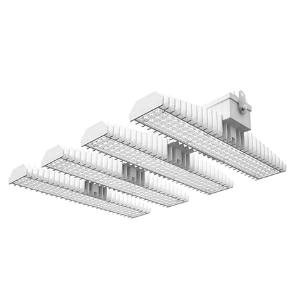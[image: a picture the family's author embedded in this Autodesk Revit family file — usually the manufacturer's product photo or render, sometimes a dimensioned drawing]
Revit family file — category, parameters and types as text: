
# Revit family: 3f_filippi_-_3f_lem_concentrato_3f_filippi_-_58890_a0811_-_3f_lem_4_led_200_cr_conc___vt_7c4e
name_source: partatom
category: Lighting Fixtures
units: mm (PartAtom-declared; Revit-internal decimal feet)

## family parameters
Cut with Voids When Loaded = No
Host = Face
Light Source = No
Part Type = Normal
Room Calculation Point = No
Round Connector Dimension = Use Diameter
Shared = No

## types (1)
- 3F Filippi - 3F LEM Concentrato (1 x LED, 30311 lm, 218 W, 4000 K)
    Apparent Load = 218 VA
    Approval mark = CE
    CIE Flux Codes = 83 96 99 100 100
    Color Rendering = 80
    Color Temperature = 4000 K
    Control Gear = Electronic ballast
    Default Elevation = 1800 mm
    Description = Industrial luminaire with high light output and high luminous efficiency designed with the most innovative technologies for environments with temperature up to 55°C.

ILLUMINOTECHNICAL
Luminous efficiency 100% (DLOR 99%, ULOR 1%).
Initial luminous flux of the luminaire 30311 lm.
Direct symmetric narrow distribution: the illuminated area has a elliptical shape.
Installation Interdistance Transv.D = 0.52 x hu - Long.D = 1.16 x hu.
Tabular UGR (CIE 117 - 4H-8H; S=0.25H; 70/50/20): RUG 17.2 - 21.
Beam angle: 31° - 73°.
Luminous efficacy 139 lm/W.
Lifetime (L93/B10): 30000 h. (tq+25°C)
Lifetime (L90/B10): 50000 h. (tq+25°C)
Lifetime (L85/B10): 80000 h. (tq+25°C)
Lifetime (L80/B10): 100000 h. (tq+25°C)
Lifetime (L85/B10): 50000 h. (tq+55°C)
Sudden decreased luminous flux after 50000 hours: 0% (C0).
Photobiological safety in compliance with IEC/TR 62778: RG0 risk exempt, (IEC 62471).
In compliance with IEC/EN 62722-2-1 - IEC/EN 62717 standards.

SOURCE
4 Mid-Power linear LED modules 50W/840.
Energy efficiency class (UE 2019/2020 - UE 2019/2015): C.
CIE 13.3 Colour rendering index: CRI >80 (R9 <50%).
IES TM-30 Fidelity Index: Rf = 84 Rg = 95.
CCT nominal colour temperature 4000 K.
Colour initial tolerance (MacAdam): SDCM 3.

MECHANICAL
Passive modular heatsinks in die-casted aluminium, painted in white colour.
To optimize the thermal management of the LED module, the heatsinks are oversized and provided with self-cleaning of cooling fins.
Wiring body in aluminium and galvanised steel anchored solidly to the sinks and thermally separated.
3F Lens lenses with high luminous efficiency, transparent methacrylate (PMMA), fixed to the LED modules.
Fixing brackets in stainless steel.
Luminaire with limited surface temperature. - D - (EN 60598-2-24)
Dimensions: 757x542 mm, height 133 mm. Weight 19.468 kg.
IP65 protection degree.
Mechanical strength to impacts IK06 (1 joule).
Glow-wire test resistance 650°C.

ELECTRICAL
Halogen Free electronic wiring 230V-50/60Hz, power factor 0.97, THD <25%, constant output current, class I, 2 driver.
Power of the luminaire 218 W.
ENEC - CE.
SAFE FLICKER: PstLM=<1 and SVM=<0.4 (IEC TR 61547-1 and IEC TR 63158), to ensure a more comfortable and safe light.
Luminaire compliant with EN 60598-2-22 for power supply from a centralised emergency system CPSS (Central Power Supply System), not incorporated in the luminaire - high risk areas excluded. The default power and flux are 100% in AC and 100% in DC.
Ambient temperature from -30°C to +55°C.
Temperature class T6 max 85°C.
Quick connection via M20 3P connector with 9-13 mm tightening range.
Power unit positioned on a separate compartment by the LED module to ensure optimum temperatures of cabling components, to be inspectable and maintainable.
Relative humidity UR: <85%.

INSTALLATION
Ceiling / Suspended / Wall.
All accessories dedicated to this product are available on the Catalog and on our website www.3F-Filippi.com.

ACCESSORIES
A0811 - VT transparent glass, tempered, not flammable, with sealing gasket.
One required for each light module. The pack contains 10 pieces.

APPLICATIONS
In commercial environments, exhibition and industrial areas, stores, open areas or with shelves.
Applications with high ambient temperature up to 55°C.
Environments in which it is necessary a total protection against falling fragments (eg environments with foodstuffs or machines with moving parts or with extreme temperature changes), use luminaires with polycarbonate lenses.

WARNING
Fixture not suitable for cold stores with an ambient temperature <0°C and/or relative humidity >85%.
Luminaire designed for disposal/recycling at end-of-life.
Replaceable (LED only) light source by a professional. Replaceable control gear by a professional.
    Height = 133 mm  [stored 0.436352 ft]
    Lamp = 1 x LED
    Lamp Light Flux = 30311 lm
    Lamp Power = 218 W
    Lamp count = 1
    Length = 757 mm
    Lifetime = 50000 h
    Luminous efficacy = 139 lm/W
    Manufacturer = 3F Filippi
    ModVariant = No
    Model = 3F Filippi - 58890+A0811 - 3F LEM 4 LED 200 CR CONC + VT
    Mounting Place = Ceiling
    Mounting Type = Pendant
    Number of Poles = 1
    OnlyDefault = Yes
    Power Factor = 1
    Product Name = 3F Filippi - 3F LEM Concentrato
    Product group = pendant luminaire
    ProductGroupID = 9
    Protection Class = Protection class I
    Protection Degree = IP 65
    RLX_Detail_Level = 1
    RLX_Emergency_Light_Flux = 0 lm
    RLX_Emergency_Type = 0
    RLX_Emergency_Type_DB = No
    RlxData = <blob elided: 118965 chars, md5=aef1443f>
    Socket = socket
    Standby Power = 0 W
    System Light Flux = 30311 lm
    System Power = 218 W
    Type Comments = Product without accessories
    Type Image = 3f_filippi_-_lem_4__a0811.jpg
    URL = http://relux.com
    VarID = ---
    Voltage = 0 V
    Weight = 0.00 kg
    Width = 542 mm

note: [stored X ft] marks values corroborated as IEEE doubles in the binary element streams (Revit-internal decimal feet)

## geometry (parser evidence)
native form markers: Blend x4, Sweep x12
no freeform markers — native parametric forms only
